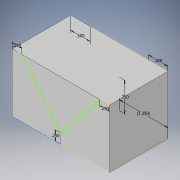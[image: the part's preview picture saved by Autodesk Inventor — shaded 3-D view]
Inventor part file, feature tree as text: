
AUTODESK INVENTOR PART (.ipt)
format: ipt  version: 2017 (Build 210142000, 142)  size: 100,864 bytes
history: native  units: in
note: dims shown in document units (in); Inventor stores cm internally (conversion verified against a paired STEP export)
features: sketch x3, extrude x1
ambient origin geometry x8: Origin, YZ Plane, XZ Plane, XY Plane, X Axis, Y Axis, Z Axis, Center Point
bodies: Solid1 (feature_tree)
feature tree (4):
  extrude  "Extrusion1"  Depth=1.5in
  sketch  "Sketch3"  dims[d2=1.5in d3=0.0in]
  sketch  "Sketch4"  dims[d4=0.25in d5=0.25in d6=0.25in d7=0.5in d8=0.5in d9=1.25in d10=0.75in]
  sketch  "Sketch1"  dims[d0=2.5in d1=1.5in]
